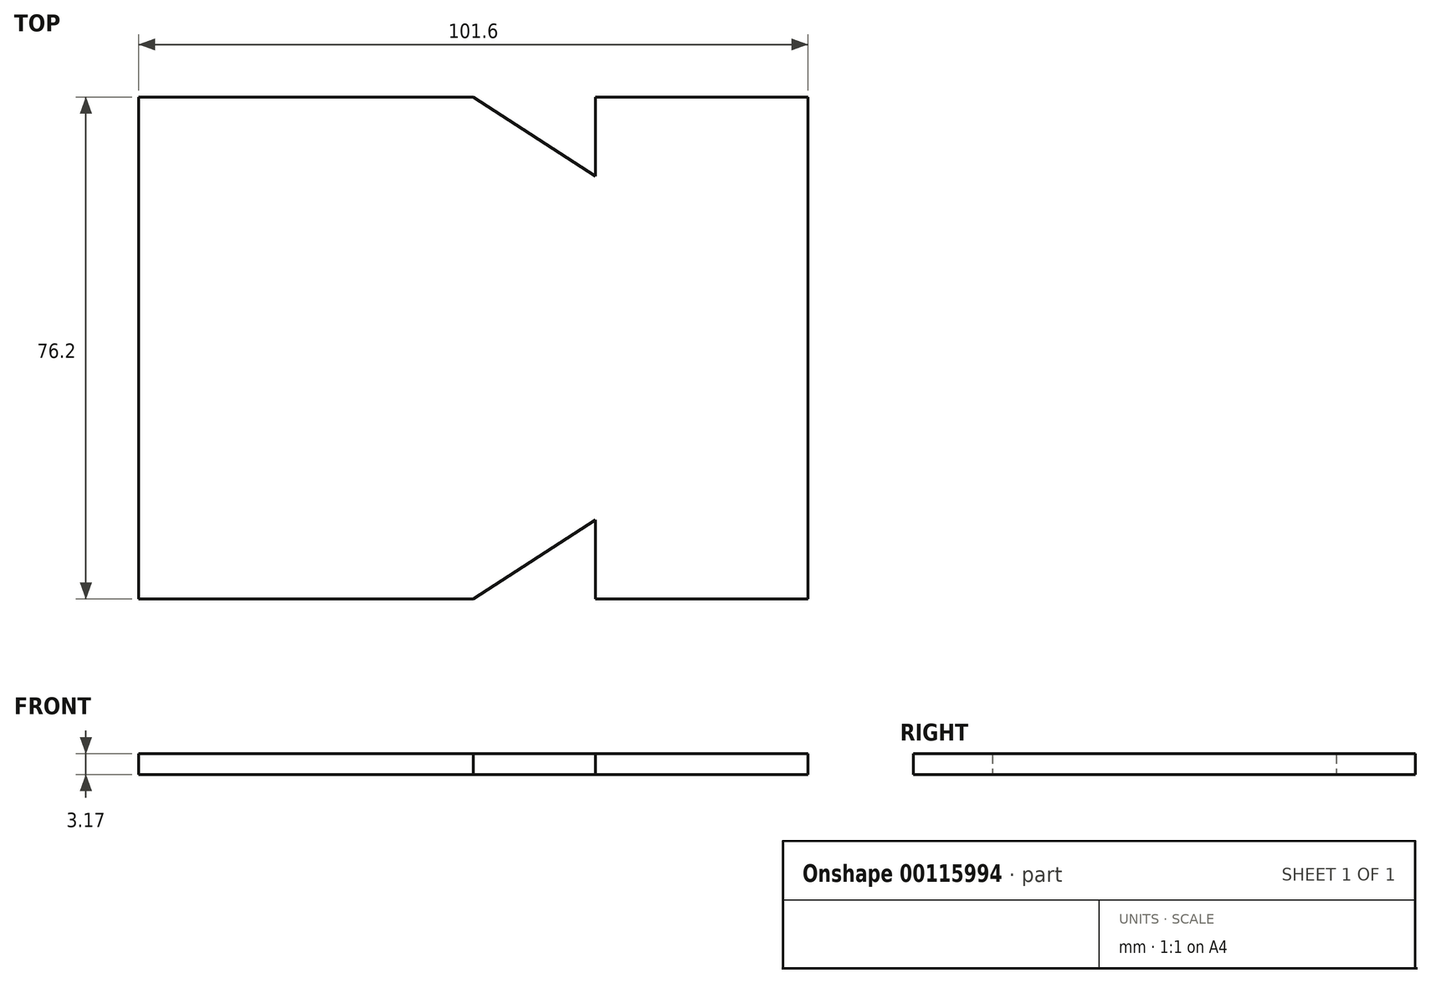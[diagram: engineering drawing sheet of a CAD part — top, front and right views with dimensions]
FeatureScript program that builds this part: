
annotation { "Feature Type Name" : "Feature", "Feature Type Description" : "" }
export const myFeature = defineFeature(function(context is Context, id is Id, definition is map)
    precondition{}
    {
        {
            var Q0;
            Q0=qCreatedBy(makeId("Top.planeOp"),FACE);
            var sketch = newSketch(context, id + "F0", { "sketchPlane" : qUnion([Q0])});
            skLineSegment(sketch, "E0", {"start": v(-69.31, 38.1) * mm, "end": v(-69.31, -38.1) * mm});
            skLineSegment(sketch, "E1", {"start": v(-69.31, -38.1) * mm, "end": v(-18.51, -38.1) * mm});
            skLineSegment(sketch, "E2", {"start": v(-69.31, 38.1) * mm, "end": v(-18.51, 38.1) * mm});
            skLineSegment(sketch, "E3", {"start": v(32.29, 38.1) * mm, "end": v(32.29, -38.1) * mm});
            skLineSegment(sketch, "E4", {"start": v(-18.51, 38.1) * mm, "end": v(0, 26.09) * mm});
            skLineSegment(sketch, "E5", {"start": v(0, 26.09) * mm, "end": v(0, 38.1) * mm});
            skLineSegment(sketch, "E6.MirrorCS", {"start": v(-18.51, -38.1) * mm, "end": v(0, -26.09) * mm});
            skLineSegment(sketch, "E7.MirrorCS", {"start": v(0, -26.09) * mm, "end": v(0, -38.1) * mm});
            skLineSegment(sketch, "E8.trimOffspring", {"start": v(0, -38.1) * mm, "end": v(32.29, -38.1) * mm});
            skLineSegment(sketch, "E9.trimOffspring", {"start": v(0, 38.1) * mm, "end": v(32.29, 38.1) * mm});
            skSolve(sketch);
        }
        {
            var Q0;
            Q0=makeQuery(id+"F0.imprint","IMPRINT",FACE,{"disambiguationData":[TD([[makeQuery(id+"F0.imprint","IMPRINT",EDGE,{"derivedFrom":sQuery(id+"F0.wireOp",EDGE,"E0")}),1.0]])]});
            extrude(context, id + "F1", {"entities" : qUnion([Q0]), "depth" : 3.17 * mm});
        }
    });
